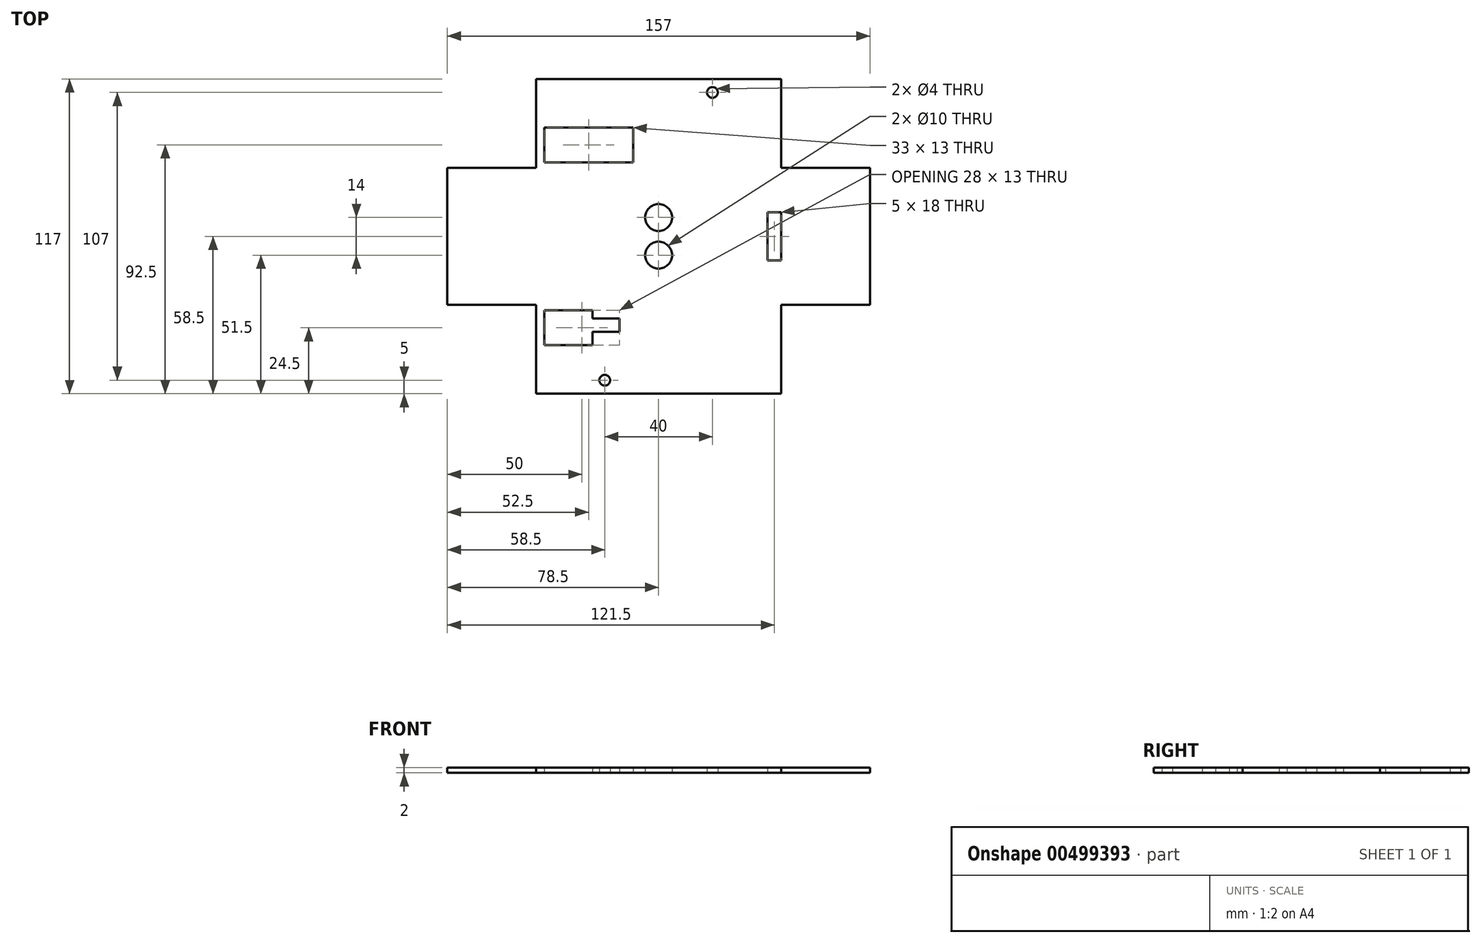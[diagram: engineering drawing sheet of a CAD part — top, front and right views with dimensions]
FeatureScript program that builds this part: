
annotation { "Feature Type Name" : "Feature", "Feature Type Description" : "" }
export const myFeature = defineFeature(function(context is Context, id is Id, definition is map)
    precondition{}
    {
        {
            var Q0;
            Q0=qCreatedBy(makeId("Top.planeOp"),FACE);
            var sketch = newSketch(context, id + "F0", { "sketchPlane" : qUnion([Q0])});
            skLineSegment(sketch, "E0.bottom", {"start": v(45.5, 25.5) * mm, "end": v(-45.5, 25.5) * mm});
            skLineSegment(sketch, "E0.top", {"start": v(45.5, -25.5) * mm, "end": v(-45.5, -25.5) * mm});
            skLineSegment(sketch, "E0.left", {"start": v(45.5, 25.5) * mm, "end": v(45.5, -25.5) * mm});
            skLineSegment(sketch, "E0.right", {"start": v(-45.5, 25.5) * mm, "end": v(-45.5, -25.5) * mm});
            skPoint(sketch, "E0.middle", {"position": v(0, 0) * mm});
            skLineSegment(sketch, "E1.bottom", {"start": v(-45.5, 25.5) * mm, "end": v(45.5, 25.5) * mm});
            skLineSegment(sketch, "E1.top", {"start": v(-45.5, 58.5) * mm, "end": v(45.5, 58.5) * mm});
            skLineSegment(sketch, "E1.left", {"start": v(-45.5, 25.5) * mm, "end": v(-45.5, 58.5) * mm});
            skLineSegment(sketch, "E1.right", {"start": v(45.5, 25.5) * mm, "end": v(45.5, 58.5) * mm});
            skLineSegment(sketch, "E2.top", {"start": v(45.5, -58.5) * mm, "end": v(-45.5, -58.5) * mm});
            skLineSegment(sketch, "E2.left", {"start": v(45.5, -25.5) * mm, "end": v(45.5, -58.5) * mm});
            skLineSegment(sketch, "E2.right", {"start": v(-45.5, -25.5) * mm, "end": v(-45.5, -58.5) * mm});
            skLineSegment(sketch, "E3.bottom", {"start": v(45.5, -25.5) * mm, "end": v(78.5, -25.5) * mm});
            skLineSegment(sketch, "E3.top", {"start": v(45.5, 25.5) * mm, "end": v(78.5, 25.5) * mm});
            skLineSegment(sketch, "E3.left", {"start": v(45.5, -25.5) * mm, "end": v(45.5, 25.5) * mm});
            skLineSegment(sketch, "E3.right", {"start": v(78.5, -25.5) * mm, "end": v(78.5, 25.5) * mm});
            skLineSegment(sketch, "E4.bottom", {"start": v(-45.5, 25.5) * mm, "end": v(-78.5, 25.5) * mm});
            skLineSegment(sketch, "E4.top", {"start": v(-45.5, -25.5) * mm, "end": v(-78.5, -25.5) * mm});
            skLineSegment(sketch, "E4.right", {"start": v(-78.5, 25.5) * mm, "end": v(-78.5, -25.5) * mm});
            skPoint(sketch, "E5", {"position": v(0, 7) * mm});
            skPoint(sketch, "E6", {"position": v(0, -7) * mm});
            skLineSegment(sketch, "E7.bottom", {"start": v(45.5, 9) * mm, "end": v(40.5, 9) * mm});
            skLineSegment(sketch, "E7.top", {"start": v(45.5, -9) * mm, "end": v(40.5, -9) * mm});
            skLineSegment(sketch, "E7.left", {"start": v(45.5, 9) * mm, "end": v(45.5, -9) * mm});
            skLineSegment(sketch, "E7.right", {"start": v(40.5, 9) * mm, "end": v(40.5, -9) * mm});
            skPoint(sketch, "E8", {"position": v(-20, -53.5) * mm});
            skPoint(sketch, "E9", {"position": v(20, 53.5) * mm});
            skLineSegment(sketch, "E10.bottom", {"start": v(-42.5, -40.5) * mm, "end": v(-24.5, -40.5) * mm});
            skLineSegment(sketch, "E10.top", {"start": v(-42.5, -27.5) * mm, "end": v(-24.5, -27.5) * mm});
            skLineSegment(sketch, "E10.left", {"start": v(-42.5, -40.5) * mm, "end": v(-42.5, -27.5) * mm});
            skLineSegment(sketch, "E10.right", {"start": v(-24.5, -40.5) * mm, "end": v(-24.5, -35.5) * mm});
            skLineSegment(sketch, "E11.bottom", {"start": v(-42.5, 40.5) * mm, "end": v(-9.5, 40.5) * mm});
            skLineSegment(sketch, "E11.top", {"start": v(-42.5, 27.5) * mm, "end": v(-9.5, 27.5) * mm});
            skLineSegment(sketch, "E11.left", {"start": v(-42.5, 40.5) * mm, "end": v(-42.5, 27.5) * mm});
            skLineSegment(sketch, "E11.right", {"start": v(-9.5, 40.5) * mm, "end": v(-9.5, 27.5) * mm});
            skLineSegment(sketch, "E12.bottom", {"start": v(-24.5, -35.5) * mm, "end": v(-14.5, -35.5) * mm});
            skLineSegment(sketch, "E12.top", {"start": v(-24.5, -30.5) * mm, "end": v(-14.5, -30.5) * mm});
            skLineSegment(sketch, "E12.right", {"start": v(-14.5, -35.5) * mm, "end": v(-14.5, -30.5) * mm});
            skLineSegment(sketch, "E13.trimOffspring", {"start": v(-24.5, -30.5) * mm, "end": v(-24.5, -27.5) * mm});
            skSolve(sketch);
        }
        {
            var Q0;
            Q0 = qSketchRegion(id + "F0", true);
            extrude(context, id + "F1", {"entities" : qUnion([Q0]), "depth" : 2 * mm});
        }
        {
            var Q0;
            Q0=sQuery(id+"F0.wireOp",VERTEX,"E8");
            var Q1;
            Q1=sQuery(id+"F0.wireOp",VERTEX,"E9");
            var Q2;
            Q2=makeQuery(id+"F1.opExtrude","SWEPT_BODY",BODY,{"disambiguationData":[OSD([sQuery(id+"F0.wireOp",EDGE,"E1.top"),sQuery(id+"F0.wireOp",EDGE,"E1.left"),sQuery(id+"F0.wireOp",EDGE,"E1.right"),sQuery(id+"F0.wireOp",EDGE,"E2.top"),sQuery(id+"F0.wireOp",EDGE,"E2.left"),sQuery(id+"F0.wireOp",EDGE,"E2.right"),sQuery(id+"F0.wireOp",EDGE,"E3.bottom"),sQuery(id+"F0.wireOp",EDGE,"E3.top"),sQuery(id+"F0.wireOp",EDGE,"E3.right"),sQuery(id+"F0.wireOp",EDGE,"E4.bottom"),sQuery(id+"F0.wireOp",EDGE,"E4.top"),sQuery(id+"F0.wireOp",EDGE,"E4.right"),sQuery(id+"F0.wireOp",EDGE,"E7.bottom"),sQuery(id+"F0.wireOp",EDGE,"E7.top"),sQuery(id+"F0.wireOp",EDGE,"E7.left"),sQuery(id+"F0.wireOp",EDGE,"E7.right"),sQuery(id+"F0.wireOp",EDGE,"d9m1lsCg-y5Xp-eJD5-57uu-5gdlZ1RXzMJy.bottom"),sQuery(id+"F0.wireOp",EDGE,"d9m1lsCg-y5Xp-eJD5-57uu-5gdlZ1RXzMJy.top"),sQuery(id+"F0.wireOp",EDGE,"d9m1lsCg-y5Xp-eJD5-57uu-5gdlZ1RXzMJy.left"),sQuery(id+"F0.wireOp",EDGE,"d9m1lsCg-y5Xp-eJD5-57uu-5gdlZ1RXzMJy.right"),sQuery(id+"F0.wireOp",EDGE,"E10.bottom"),sQuery(id+"F0.wireOp",EDGE,"E10.top"),sQuery(id+"F0.wireOp",EDGE,"E10.left"),sQuery(id+"F0.wireOp",EDGE,"E10.right"),sQuery(id+"F0.wireOp",EDGE,"E11.bottom"),sQuery(id+"F0.wireOp",EDGE,"E11.top"),sQuery(id+"F0.wireOp",EDGE,"E11.left"),sQuery(id+"F0.wireOp",EDGE,"E11.right")])]});
            hole(context, id + "F2", {"style" : HoleStyle.SIMPLE, "endStyle" : HoleEndStyle.THROUGH, "oppositeDirection" : true, "holeDiameter" : 4 * mm, "isTappedThrough" : true, "tappedDepth" : 12 * mm, "tapClearance" : 3, "startFromSketch" : true, "locations" : qUnion([Q0, Q1]), "scope" : qUnion([Q2])});
        }
        {
            var Q0;
            Q0=sQuery(id+"F0.wireOp",VERTEX,"E5");
            var Q1;
            Q1=sQuery(id+"F0.wireOp",VERTEX,"E6");
            var Q2;
            Q2=makeQuery(id+"F1.opExtrude","SWEPT_BODY",BODY,{"disambiguationData":[OSD([sQuery(id+"F0.wireOp",EDGE,"E1.top"),sQuery(id+"F0.wireOp",EDGE,"E1.left"),sQuery(id+"F0.wireOp",EDGE,"E1.right"),sQuery(id+"F0.wireOp",EDGE,"E2.top"),sQuery(id+"F0.wireOp",EDGE,"E2.left"),sQuery(id+"F0.wireOp",EDGE,"E2.right"),sQuery(id+"F0.wireOp",EDGE,"E3.bottom"),sQuery(id+"F0.wireOp",EDGE,"E3.top"),sQuery(id+"F0.wireOp",EDGE,"E3.right"),sQuery(id+"F0.wireOp",EDGE,"E4.bottom"),sQuery(id+"F0.wireOp",EDGE,"E4.top"),sQuery(id+"F0.wireOp",EDGE,"E4.right"),sQuery(id+"F0.wireOp",EDGE,"E7.bottom"),sQuery(id+"F0.wireOp",EDGE,"E7.top"),sQuery(id+"F0.wireOp",EDGE,"E7.left"),sQuery(id+"F0.wireOp",EDGE,"E7.right"),sQuery(id+"F0.wireOp",EDGE,"d9m1lsCg-y5Xp-eJD5-57uu-5gdlZ1RXzMJy.bottom"),sQuery(id+"F0.wireOp",EDGE,"d9m1lsCg-y5Xp-eJD5-57uu-5gdlZ1RXzMJy.top"),sQuery(id+"F0.wireOp",EDGE,"d9m1lsCg-y5Xp-eJD5-57uu-5gdlZ1RXzMJy.left"),sQuery(id+"F0.wireOp",EDGE,"d9m1lsCg-y5Xp-eJD5-57uu-5gdlZ1RXzMJy.right"),sQuery(id+"F0.wireOp",EDGE,"E10.bottom"),sQuery(id+"F0.wireOp",EDGE,"E10.top"),sQuery(id+"F0.wireOp",EDGE,"E10.left"),sQuery(id+"F0.wireOp",EDGE,"E10.right"),sQuery(id+"F0.wireOp",EDGE,"E11.bottom"),sQuery(id+"F0.wireOp",EDGE,"E11.top"),sQuery(id+"F0.wireOp",EDGE,"E11.left"),sQuery(id+"F0.wireOp",EDGE,"E11.right")])]});
            hole(context, id + "F3", {"style" : HoleStyle.SIMPLE, "endStyle" : HoleEndStyle.THROUGH, "oppositeDirection" : true, "holeDiameter" : 10 * mm, "isTappedThrough" : true, "tappedDepth" : 12 * mm, "tapClearance" : 3, "startFromSketch" : true, "locations" : qUnion([Q0, Q1]), "scope" : qUnion([Q2])});
        }
    });
